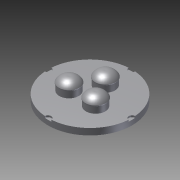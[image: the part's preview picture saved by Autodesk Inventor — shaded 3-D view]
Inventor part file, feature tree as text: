
AUTODESK INVENTOR PART (.ipt)
format: ipt  version: 2012 (Build 160160000, 160)  size: 209,408 bytes
history: native  units: mm
features: extrude x5, sketch x5, fillet x2, projected_geometry x2
ambient origin geometry x8: Origin, YZ Plane, XZ Plane, XY Plane, X Axis, Y Axis, Z Axis, Center Point
bodies: Solid1 (feature_tree)
feature tree (14):
  extrude  "Extrusion1"  Depth=2.0mm TaperAngle=0.0deg
  extrude  "Extrusion2"  Depth=6.0mm
  extrude  "Extrusion3"  Depth=6.0mm
  fillet  "Fillet1"  Radius=2.0mm
  fillet  "Fillet2"  Radius=6.6mm
  extrude  "Extrusion7"  Depth=6.6mm
  extrude  "Extrusion8"  Depth=3.175mm
  sketch  "Sketch3"  dims[d0=26.0mm d1=2.0mm d2=0.0mm]
  sketch  "Sketch4"  dims[d3=9.5mm d4=6.0mm]
  sketch  "Sketch5"  dims[d5=6.0mm d6=6.0mm d7=2.0mm d8=0.0mm d9=6.6mm]
  projected_geometry  "Projected Loop1"
  projected_geometry  "Projected Loop2"
  sketch  "Sketch9"  dims[d10=6.6mm d11=6.6mm]
  sketch  "Sketch11"  dims[d12=2.0mm d13=0.0mm d14=3.175mm d15=0.25mm d25=1.8mm d26=10.0mm d27=0.0mm d32=2.0mm d33=2.0mm d34=2.0mm d35=2.0mm d36=0.5mm d37=0.0mm]
